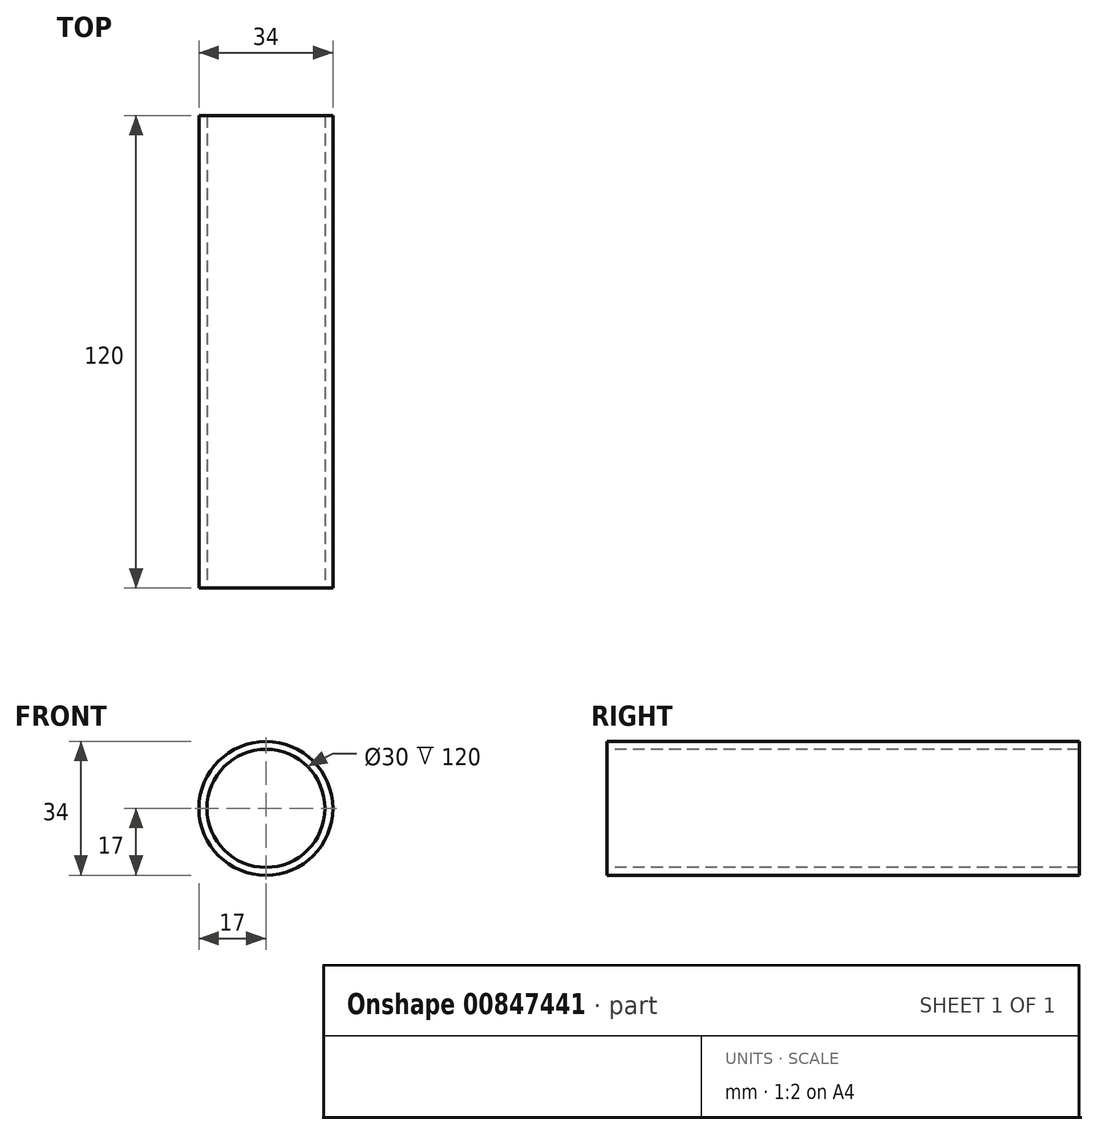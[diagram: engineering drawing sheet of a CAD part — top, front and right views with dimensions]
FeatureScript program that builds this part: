
annotation { "Feature Type Name" : "Feature", "Feature Type Description" : "" }
export const myFeature = defineFeature(function(context is Context, id is Id, definition is map)
    precondition{}
    {
        {
            var Q0;
            Q0=qCreatedBy(makeId("Front.planeOp"),FACE);
            var sketch = newSketch(context, id + "F0", { "sketchPlane" : qUnion([Q0])});
            skLineSegment(sketch, "E0", {"start": v(0, 40.58) * mm, "end": v(0, -41.33) * mm, "construction": true});
            skLineSegment(sketch, "E1", {"start": v(-47.51, 0) * mm, "end": v(52.14, 0) * mm, "construction": true});
            skCircle(sketch, "E2", {"center": v(0, 0) * mm, "radius": 17 * mm});
            skCircle(sketch, "E3.0", {"center": v(0, 0) * mm, "radius": 15 * mm});
            skSolve(sketch);
        }
        {
            var Q0;
            Q0=qSketchRegion(id+"F0",true);
            extrude(context, id + "F1", {"entities" : qUnion([Q0]), "oppositeDirection" : true, "depth" : 120 * mm, "offsetDistance" : 25 * mm});
        }
    });
